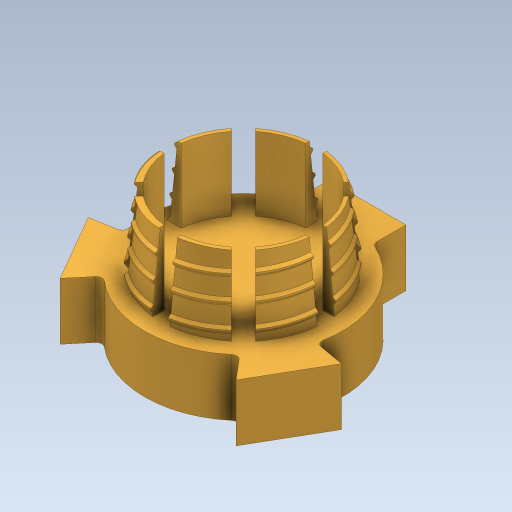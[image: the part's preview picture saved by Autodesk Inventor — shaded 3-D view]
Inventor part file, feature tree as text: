
AUTODESK INVENTOR PART (.ipt)
format: ipt  version: 2023 (Build 270158000, 158)  size: 960,000 bytes
history: native  units: mm
features: sketch x5, extrude x4, helix x2, draft x1, direct_edit x1, fillet x1, other x1
ambient origin geometry x8: Origin, YZ Plane, XZ Plane, XY Plane, X Axis, Y Axis, Z Axis, Center Point
bodies: Solid1 (feature_tree)
feature tree (15):
  extrude  "Extrusion1"  Depth=26.5mm
  draft  "FaceDraft1"
  sketch  "Sketch2"  dims[d34=0.0mm d35=0.0mm d56=8.726646mm]
  helix  "Coil3"  [1 undecoded]
  helix  "Coil4"  [1 undecoded]
  direct_edit  "Direct Edit2"
  extrude  "Extrusion2"  Depth=8.726646mm
  extrude  "Extrusion13"  TaperAngle=90.0deg  [1 undecoded]
  extrude  "Extrusion14"  Depth=1.0mm
  fillet  "Fillet10"  [1 undecoded]
  sketch  "Sketch1"  dims[d0=25.0mm d1=26.5mm d2=12.875mm d3=0.0mm d4=1.047198mm]
  sketch  "Sketch3"  dims[d62=4.0mm d63=13.0mm d64=10.0mm d65=1.047198mm]
  sketch  "Sketch10"  dims[d66=90.0deg d67=90.0deg d68=0.0mm d69=0.0mm d70=4.0mm d71=3.0mm d72=10.0mm d73=-1.047198mm d74=90.0deg d75=90.0deg d76=0.0mm d77=0.0mm]
  sketch  "Sketch11"  dims[d79=-0.127mm d145=34.58632mm d150=120.0deg d151=120.0deg d152=13.5mm d153=21.6866mm d154=12.217305mm d155=21.6866mm d156=13.5mm d157=10.0mm d158=0.0mm d159=3.0mm d160=80.0mm d162=360.0deg d164=0.0mm d165=0.0mm d166=1.0mm d109=0.5mm d110=0.872665mm d111=0.5mm d112=0.872665mm]
  other  "Size2"
note: 4 required parameter values undecoded (feature->parameter linkage not recoverable at this tier; creation-order binding heuristic only, values carry confidence <= 0.55)
